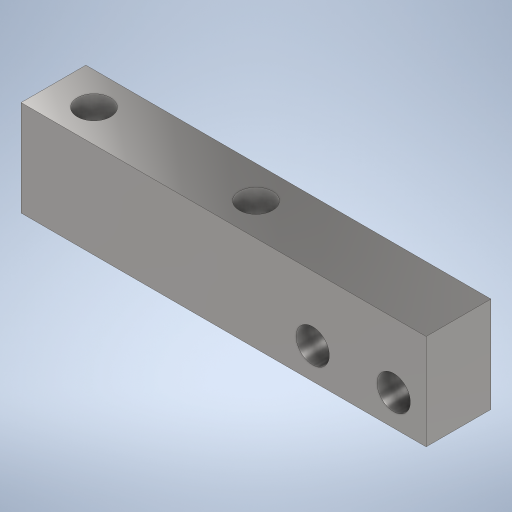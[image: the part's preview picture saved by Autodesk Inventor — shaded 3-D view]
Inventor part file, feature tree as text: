
AUTODESK INVENTOR PART (.ipt)
format: ipt  version: 2023 (Build 270158000, 158)  size: 254,976 bytes
history: native  units: mm
features: extrude x4, sketch x4
ambient origin geometry x8: Origin, YZ Plane, XZ Plane, XY Plane, X Axis, Y Axis, Z Axis, Center Point
bodies: Solid1 (feature_tree)
feature tree (8):
  extrude  "Extrusion1"  Depth=15.0mm
  extrude  "Extrusion2"  Depth=10.0mm
  extrude  "Extrusion3"  Depth=2.0mm
  extrude  "Extrusion4"  Depth=4.0mm
  sketch  "Sketch1"  dims[d0=5.9mm d1=15.0mm]
  sketch  "Sketch2"  dims[d2=4.0mm d3=0.0mm d4=10.0mm]
  sketch  "Sketch3"  dims[d5=2.5mm d6=2.0mm]
  sketch  "Sketch4"  dims[d7=2.0mm d8=2.05mm d9=2.05mm d10=8.0mm d11=0.0mm d12=10.0mm d13=4.0mm d14=0.0mm d15=2.05mm d16=5.9mm d17=4.0mm d18=4.0mm d19=5.0mm d20=2.0mm d21=2.05mm d22=2.05mm d23=4.0mm d24=0.0mm]
